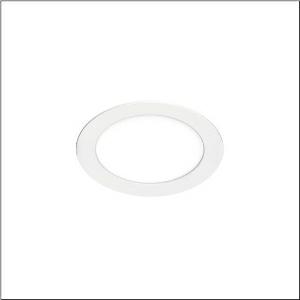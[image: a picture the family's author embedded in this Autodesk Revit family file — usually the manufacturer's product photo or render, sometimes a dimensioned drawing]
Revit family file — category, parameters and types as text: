
# Revit family: lunis_41_flat_51dr10mfgcb
name_source: partatom
category: Lighting Fixtures
units: mm (PartAtom-declared; Revit-internal decimal feet)

## family parameters
Cut with Voids When Loaded = No
Host = Face
Light Source = No
Part Type = Normal
Room Calculation Point = No
Round Connector Dimension = Use Diameter
Shared = No

## types (1)
- --- (1 x LED, 2430 lm, 19.5 W, 4000K)
    Apparent Load = 20 VA
    CIE Flux Codes = 49 80 96 100 100
    Color Rendering = 80
    Color Temperature = 4000K
    Default Elevation = 1800 mm
    Description = Lunis 41,  Flat, downlight, light emission: direct distribution, LED rated luminous flux: 2.360lm, light colour: 830/840, mains connection: 230V, AC, 50/60Hz, housing, round, of aluminium, coated, traffic white (RAL 9016), diameter: 225mm, protection rating (complete): IP20, protection rating (on room side): IP44, insulation class (complete): insulation class II (safety insulation), certification: CE, permissible ambient temperature for indoor applications: -20..+40°C, packaging unit: 1 piece
    Height = 0 mm  [stored 0 ft]
    Lamp = 1 x LED
    Lamp Light Flux = 2430 lm
    Lamp Power = 19.5 W
    Lamp count = 1
    Length = 225 mm
    Luminous efficacy = 125 lm/W
    Manufacturer = Siteco
    ModVariant = No
    Model = 51DR10MFGCB
    Mounting Place = Ceiling
    Mounting Type = Recessed
    Number of Poles = 1
    OnlyDefault = Yes
    Power Factor = 1
    Product Name = Lunis 41 Flat
    Product group = downlight
    ProductGroupID = 401
    Protection Class = Protection class II
    Protection Degree = IP 20
    RLX_Detail_Level = 1
    RLX_Emergency_Light_Flux = 0 lm
    RLX_Emergency_Type = 0
    RLX_Emergency_Type_DB = No
    RlxData = <blob elided: 11573 chars, md5=8ceb9450>
    Socket = socket
    Standby Power = 0 W
    System Light Flux = 2430 lm
    System Power = 20 W
    Type Comments = factory setting: colour temperature 4000K
    Type Image = l_1340923.jpg
    URL = http://relux.com
    VarID = @adj_002219
    Voltage = 0 V
    Weight = 0.00 kg
    Width = 0 mm  [stored 0 ft]

note: [stored X ft] marks values corroborated as IEEE doubles in the binary element streams (Revit-internal decimal feet)

## geometry (parser evidence)
native form markers: Sweep x10
no freeform markers — native parametric forms only
